# Revit family: QF_Vollrath_59508DW_cat
name_source: partatom
category: Specialty Equipment
revit_build: Autodesk Revit 2016 (Build: 20151007_0715(x64)
units: mm (PartAtom-declared; Revit-internal decimal feet)

## family parameters
Always vertical = Yes
Cut with Voids When Loaded = Yes
OmniClass Number = 23.40.40.00
OmniClass Title = Food Service Equipment and Furnishings
Part Type = Normal
Room Calculation Point = No
Round Connector Dimension = Use Diameter
Shared = No
Work Plane-Based = Yes

## types (1)
- QF_Vollrath_59508DW_cat
    Apparent Power = 378 VA
    Conn Plug = NEMA 5-15P
    Cycle = 50 Hz
    Default Elevation = 36"
    Depth = 16"
    Description = Buffet Induction Warmer
    Elec Conn Connection Height = 0"
    FL Amps = 3 A
    Foodservice Equipment Identifier = Yes
    Manufacturer = Vollrath
    Model = 59508DW
    Phase = 1
    Volts = 120 V
    Watts = 375 W
    Weight in Pounds = 14.9
    Width = 23"

## geometry (parser evidence)
native form markers: Sweep x4
no freeform markers — native parametric forms only
